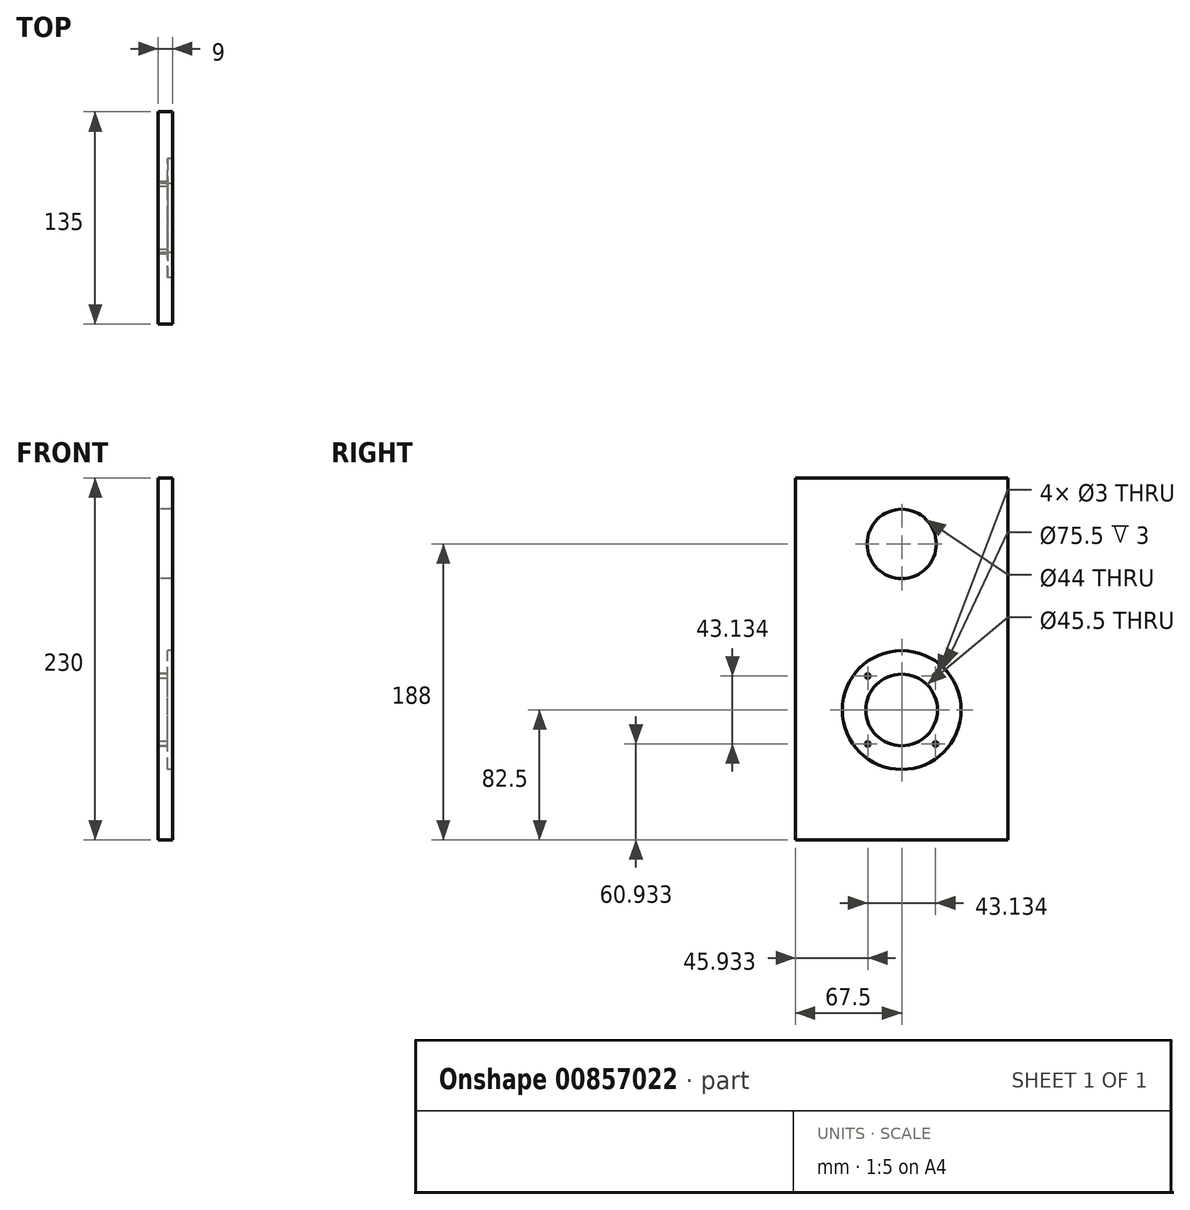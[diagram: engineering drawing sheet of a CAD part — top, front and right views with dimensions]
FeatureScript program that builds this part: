
annotation { "Feature Type Name" : "Feature", "Feature Type Description" : "" }
export const myFeature = defineFeature(function(context is Context, id is Id, definition is map)
    precondition{}
    {
        {
            var Q0;
            Q0=qCreatedBy(makeId("Right.planeOp"),FACE);
            var sketch = newSketch(context, id + "F0", { "sketchPlane" : qUnion([Q0])});
            skLineSegment(sketch, "E0.bottom", {"start": v(-67.5, 115) * mm, "end": v(67.5, 115) * mm});
            skLineSegment(sketch, "E0.top", {"start": v(-67.5, -115) * mm, "end": v(67.5, -115) * mm});
            skLineSegment(sketch, "E0.left", {"start": v(-67.5, 115) * mm, "end": v(-67.5, -115) * mm});
            skLineSegment(sketch, "E0.right", {"start": v(67.5, 115) * mm, "end": v(67.5, -115) * mm});
            skLineSegment(sketch, "E1", {"start": v(0, 115) * mm, "end": v(0, -115) * mm});
            skPoint(sketch, "E2", {"position": v(0, -97.5) * mm});
            skPoint(sketch, "E3", {"position": v(0, -32.5) * mm});
            skCircle(sketch, "E4", {"center": v(0, 73) * mm, "radius": 22 * mm});
            skCircle(sketch, "E5", {"center": v(0, 73) * mm, "radius": 16.5 * mm});
            skCircle(sketch, "E6", {"center": v(0, -32.5) * mm, "radius": 22.75 * mm});
            skCircle(sketch, "E7", {"center": v(0, -32.5) * mm, "radius": 37.75 * mm});
            skCircle(sketch, "E8", {"center": v(-21.57, -10.93) * mm, "radius": 1.5 * mm});
            skCircle(sketch, "E9.1.0", {"center": v(-21.57, -54.07) * mm, "radius": 1.5 * mm});
            skCircle(sketch, "E9.2.0", {"center": v(21.57, -54.07) * mm, "radius": 1.5 * mm});
            skCircle(sketch, "E9.3.0", {"center": v(21.57, -10.93) * mm, "radius": 1.5 * mm});
            skSolve(sketch);
        }
        {
            var Q0;
            {var subQ12=sQuery(id+"F0.wireOp",EDGE,"E0.left");Q0=makeQuery(id+"F0.imprint","IMPRINT",FACE,{"disambiguationData":[TD([[makeQuery(id+"F0.imprint","IMPRINT",EDGE,{"derivedFrom":subQ12}),1.0]])]});}
            var Q1;
            {var subQ11=sQuery(id+"F0.wireOp",EDGE,"E0.right");Q1=makeQuery(id+"F0.imprint","IMPRINT",FACE,{"disambiguationData":[TD([[makeQuery(id+"F0.imprint","IMPRINT",EDGE,{"derivedFrom":subQ11}),-1.0]])]});}
            extrude(context, id + "F1", {"entities" : qUnion([Q0, Q1]), "depth" : 9 * mm, "offsetDistance" : 25 * mm});
        }
        {
            var Q0;
            {var subQ0=sQuery(id+"F0.wireOp",EDGE,"E4");var subQ1=sQuery(id+"F0.wireOp",EDGE,"E1");var subQ2=makeQuery(id+"F0.imprint","INTERSECT",VERTEX,{"disambiguationData":[OD(0.0)],"derivedFrom":[subQ1,subQ0]});Q0=makeQuery(id+"F0.imprint","IMPRINT",FACE,{"disambiguationData":[TD([[makeQuery(id+"F0.imprint","IMPRINT",EDGE,{"disambiguationData":[TD([[subQ2,-1.0]])],"derivedFrom":subQ1}),-1.0]])]});}
            var Q1;
            {var subQ0=sQuery(id+"F0.wireOp",EDGE,"E4");var subQ1=sQuery(id+"F0.wireOp",EDGE,"E1");var subQ2=makeQuery(id+"F0.imprint","INTERSECT",VERTEX,{"disambiguationData":[OD(0.0)],"derivedFrom":[subQ1,subQ0]});Q1=makeQuery(id+"F0.imprint","IMPRINT",FACE,{"disambiguationData":[TD([[makeQuery(id+"F0.imprint","IMPRINT",EDGE,{"disambiguationData":[TD([[subQ2,-1.0]])],"derivedFrom":subQ1}),1.0]])]});}
            var Q2;
            {var subQ5=sQuery(id+"F0.wireOp",EDGE,"E1");var subQ9=sQuery(id+"F0.wireOp",EDGE,"E7");var subQ11=makeQuery(id+"F0.imprint","INTERSECT",VERTEX,{"disambiguationData":[OD(0.0)],"derivedFrom":[subQ5,subQ9]});Q2=makeQuery(id+"F0.imprint","IMPRINT",FACE,{"disambiguationData":[TD([[makeQuery(id+"F0.imprint","IMPRINT",EDGE,{"disambiguationData":[TD([[subQ11,-1.0]])],"derivedFrom":subQ5}),-1.0]])]});}
            var Q3;
            {var subQ1=sQuery(id+"F0.wireOp",EDGE,"E1");var subQ5=sQuery(id+"F0.wireOp",EDGE,"E6");var subQ6=makeQuery(id+"F0.imprint","INTERSECT",VERTEX,{"disambiguationData":[OD(1.0)],"derivedFrom":[subQ1,subQ5]});Q3=makeQuery(id+"F0.imprint","IMPRINT",FACE,{"disambiguationData":[TD([[makeQuery(id+"F0.imprint","IMPRINT",EDGE,{"disambiguationData":[TD([[subQ6,-1.0]])],"derivedFrom":subQ1}),-1.0]])]});}
            var Q4;
            {var subQ1=sQuery(id+"F0.wireOp",EDGE,"3XiGr47N-JLnz-w9pF-kUHc-UIBYfuox3lXp");var subQ5=sQuery(id+"F0.wireOp",EDGE,"E1");var subQ6=makeQuery(id+"F0.imprint","INTERSECT",VERTEX,{"disambiguationData":[OD(0.0)],"derivedFrom":[subQ5,subQ1]});Q4=makeQuery(id+"F0.imprint","IMPRINT",FACE,{"disambiguationData":[TD([[makeQuery(id+"F0.imprint","IMPRINT",EDGE,{"disambiguationData":[TD([[subQ6,-1.0]])],"derivedFrom":subQ5}),-1.0]])]});}
            var Q5;
            {var subQ1=sQuery(id+"F0.wireOp",EDGE,"E1");var subQ5=sQuery(id+"F0.wireOp",EDGE,"E7");var subQ6=makeQuery(id+"F0.imprint","INTERSECT",VERTEX,{"disambiguationData":[OD(0.0)],"derivedFrom":[subQ1,subQ5]});Q5=makeQuery(id+"F0.imprint","IMPRINT",FACE,{"disambiguationData":[TD([[makeQuery(id+"F0.imprint","IMPRINT",EDGE,{"disambiguationData":[TD([[subQ6,-1.0]])],"derivedFrom":subQ1}),1.0]])]});}
            var Q6;
            {var subQ0=sQuery(id+"F0.wireOp",EDGE,"3XiGr47N-JLnz-w9pF-kUHc-UIBYfuox3lXp");var subQ1=sQuery(id+"F0.wireOp",EDGE,"E1");var subQ2=makeQuery(id+"F0.imprint","INTERSECT",VERTEX,{"disambiguationData":[OD(0.0)],"derivedFrom":[subQ1,subQ0]});Q6=makeQuery(id+"F0.imprint","IMPRINT",FACE,{"disambiguationData":[TD([[makeQuery(id+"F0.imprint","IMPRINT",EDGE,{"disambiguationData":[TD([[subQ2,-1.0]])],"derivedFrom":subQ1}),1.0]])]});}
            extrude(context, id + "F2", {"entities" : qUnion([Q0, Q1, Q2, Q3, Q4, Q5, Q6]), "operationType" : NewBodyOperationType.ADD, "depth" : 6 * mm, "offsetDistance" : 25 * mm});
        }
    });
